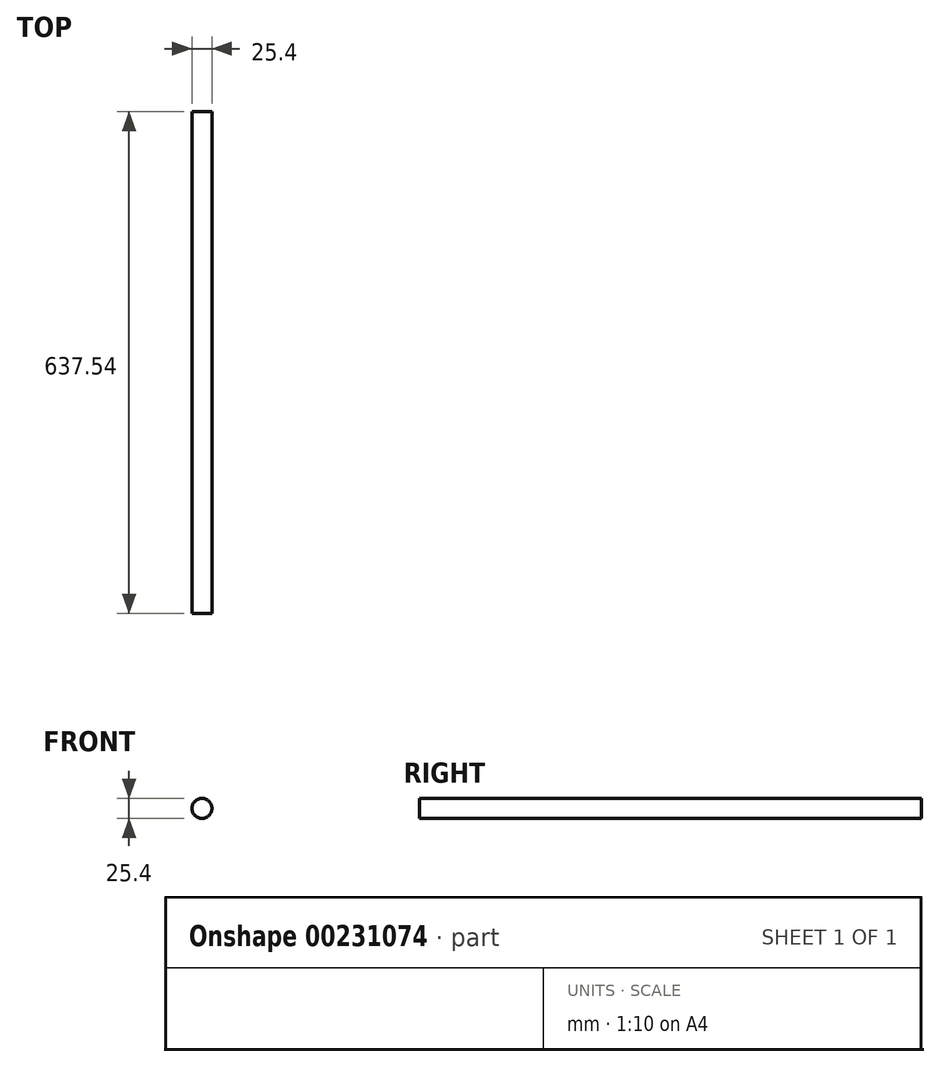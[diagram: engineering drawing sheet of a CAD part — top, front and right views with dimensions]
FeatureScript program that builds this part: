
annotation { "Feature Type Name" : "Feature", "Feature Type Description" : "" }
export const myFeature = defineFeature(function(context is Context, id is Id, definition is map)
    precondition{}
    {
        {
            var Q0;
            Q0=qCreatedBy(makeId("Front.planeOp"),FACE);
            var sketch = newSketch(context, id + "F0", { "sketchPlane" : qUnion([Q0])});
            skCircle(sketch, "E0", {"center": v(0, 0) * mm, "radius": 12.7 * mm});
            skSolve(sketch);
        }
        {
            var Q0;
            Q0 = qSketchRegion(id + "F0", true);
            extrude(context, id + "F1", {"entities" : qUnion([Q0]), "depth" : 637.54 * mm});
        }
    });
